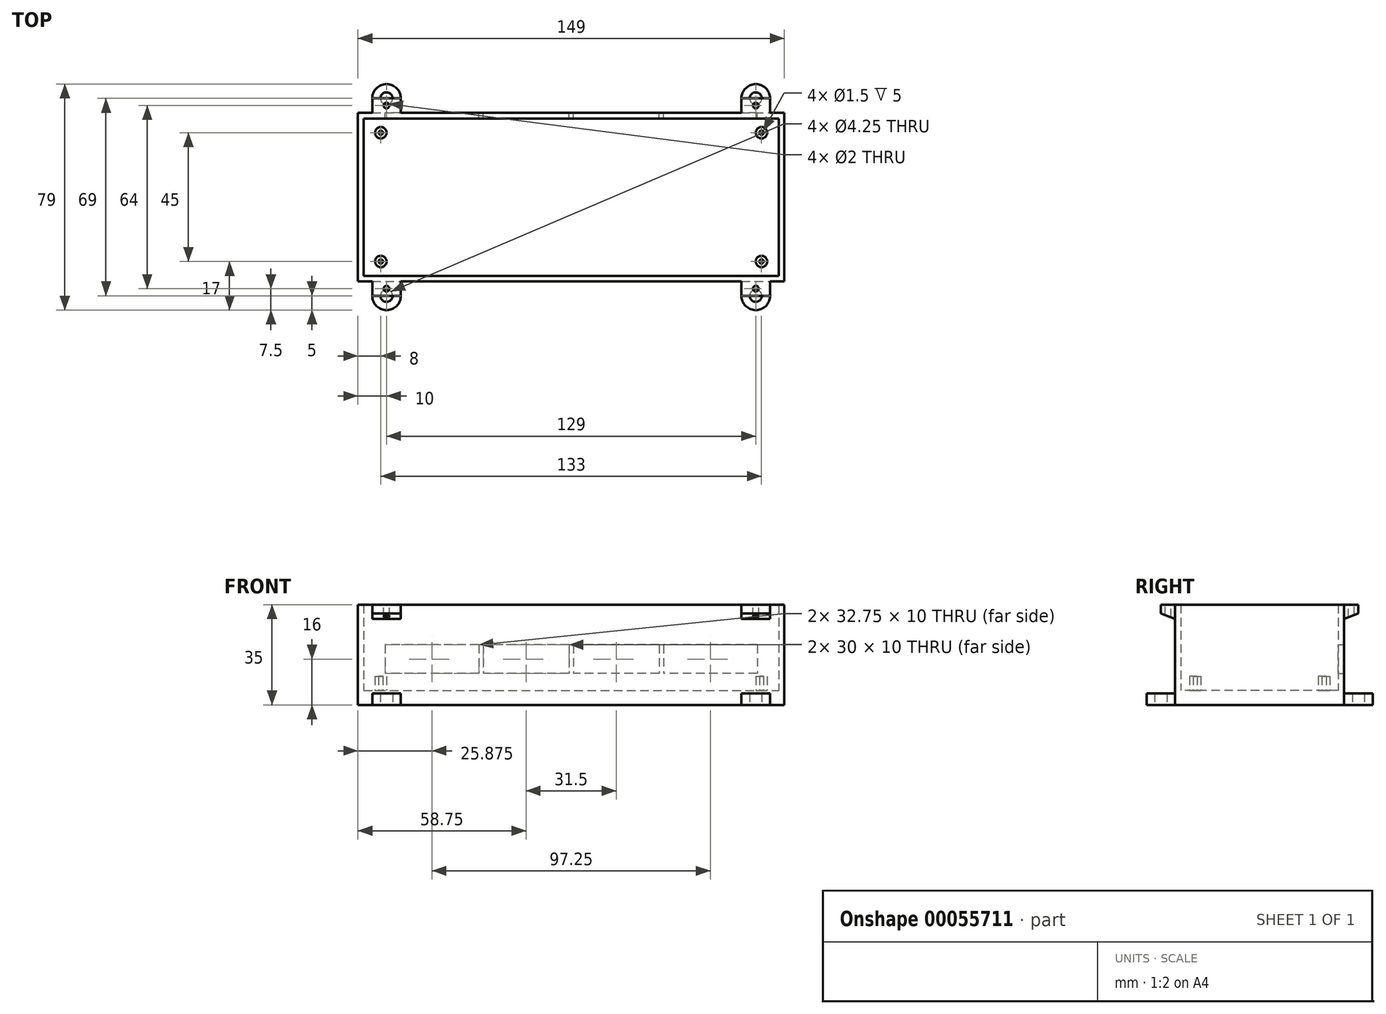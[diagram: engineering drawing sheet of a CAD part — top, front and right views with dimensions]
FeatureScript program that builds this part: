
annotation { "Feature Type Name" : "Feature", "Feature Type Description" : "" }
export const myFeature = defineFeature(function(context is Context, id is Id, definition is map)
    precondition{}
    {
        {
            var Q0;
            Q0=qCreatedBy(makeId("Top.planeOp"),FACE);
            var sketch = newSketch(context, id + "F0", { "sketchPlane" : qUnion([Q0])});
            skLineSegment(sketch, "E0.bottom", {"start": v(-72.5, 27.5) * mm, "end": v(72.5, 27.5) * mm});
            skLineSegment(sketch, "E0.top", {"start": v(-72.5, -27.5) * mm, "end": v(72.5, -27.5) * mm});
            skLineSegment(sketch, "E0.left", {"start": v(-72.5, 27.5) * mm, "end": v(-72.5, -27.5) * mm});
            skLineSegment(sketch, "E0.right", {"start": v(72.5, 27.5) * mm, "end": v(72.5, -27.5) * mm});
            skPoint(sketch, "E0.middle", {"position": v(0, 0) * mm});
            skLineSegment(sketch, "E1.bottom", {"start": v(-74.5, 29.5) * mm, "end": v(74.5, 29.5) * mm});
            skLineSegment(sketch, "E1.top", {"start": v(-74.5, -29.5) * mm, "end": v(74.5, -29.5) * mm});
            skLineSegment(sketch, "E1.left", {"start": v(-74.5, 29.5) * mm, "end": v(-74.5, -29.5) * mm});
            skLineSegment(sketch, "E1.right", {"start": v(74.5, 29.5) * mm, "end": v(74.5, -29.5) * mm});
            skSolve(sketch);
        }
        {
            var Q0;
            Q0=makeQuery(id+"F0.imprint","IMPRINT",FACE,{"disambiguationData":[TD([[makeQuery(id+"F0.imprint","IMPRINT",EDGE,{"derivedFrom":sQuery(id+"F0.wireOp",EDGE,"E0.bottom")}),1.0]])]});
            extrude(context, id + "F1", {"entities" : qUnion([Q0]), "depth" : 30 * mm});
        }
        {
            var Q0;
            Q0=makeQuery(id+"F1.opExtrude","CAP_FACE",FACE,{"disambiguationData":[OSD([sQuery(id+"F0.wireOp",EDGE,"E0.bottom"),sQuery(id+"F0.wireOp",EDGE,"E0.top"),sQuery(id+"F0.wireOp",EDGE,"E0.left"),sQuery(id+"F0.wireOp",EDGE,"E0.right"),sQuery(id+"F0.wireOp",EDGE,"E1.bottom"),sQuery(id+"F0.wireOp",EDGE,"E1.top"),sQuery(id+"F0.wireOp",EDGE,"E1.left"),sQuery(id+"F0.wireOp",EDGE,"E1.right")])],"isStart":true});
            var sketch = newSketch(context, id + "F2", { "sketchPlane" : qUnion([Q0])});
            skLineSegment(sketch, "E2.0.0", {"start": v(-74.5, -29.5) * mm, "end": v(74.5, -29.5) * mm});
            skLineSegment(sketch, "E2.0.1", {"start": v(74.5, -29.5) * mm, "end": v(74.5, 29.5) * mm});
            skLineSegment(sketch, "E2.0.2", {"start": v(74.5, 29.5) * mm, "end": v(-74.5, 29.5) * mm});
            skLineSegment(sketch, "E2.0.3", {"start": v(-74.5, 29.5) * mm, "end": v(-74.5, -29.5) * mm});
            skSolve(sketch);
        }
        {
            var Q0;
            Q0=makeQuery(id+"F2.imprint","IMPRINT",FACE,{"disambiguationData":[TD([[makeQuery(id+"F2.imprint","IMPRINT",EDGE,{"derivedFrom":sQuery(id+"F2.wireOp",EDGE,"E2.0.0")}),1.0]])]});
            var Q1;
            Q1=makeQuery(id+"F2.imprint","IMPRINT",FACE,{"disambiguationData":[TD([[makeQuery(id+"F2.imprint","IMPRINT",EDGE,{"derivedFrom":makeQuery(id+"F1.opExtrude","CAP_EDGE",EDGE,{"disambiguationData":[OSD([sQuery(id+"F0.wireOp",EDGE,"E0.bottom")])],"isStart":true})}),1.0]])]});
            extrude(context, id + "F3", {"entities" : qUnion([Q0, Q1]), "operationType" : NewBodyOperationType.ADD, "depth" : 5 * mm});
        }
        {
            var Q0;
            Q0=makeQuery(id+"F3.opExtrude","CAP_FACE",FACE,{"disambiguationData":[OSD([sQuery(id+"F2.wireOp",EDGE,"E2.0.0"),sQuery(id+"F2.wireOp",EDGE,"E2.0.1"),sQuery(id+"F2.wireOp",EDGE,"E2.0.2"),sQuery(id+"F2.wireOp",EDGE,"E2.0.3")])],"isStart":true});
            var sketch = newSketch(context, id + "F4", { "sketchPlane" : qUnion([Q0])});
            skLineSegment(sketch, "E3.bottom", {"start": v(-64.5, 22.5) * mm, "end": v(64.5, 22.5) * mm, "construction": true});
            skLineSegment(sketch, "E3.top", {"start": v(-64.5, -22.5) * mm, "end": v(64.5, -22.5) * mm, "construction": true});
            skLineSegment(sketch, "E3.left", {"start": v(-64.5, 22.5) * mm, "end": v(-64.5, -22.5) * mm, "construction": true});
            skLineSegment(sketch, "E3.right", {"start": v(64.5, 22.5) * mm, "end": v(64.5, -22.5) * mm, "construction": true});
            skPoint(sketch, "E3.middle", {"position": v(0, 0) * mm});
            skLineSegment(sketch, "E4.bottom", {"start": v(-66.5, 22.5) * mm, "end": v(66.5, 22.5) * mm, "construction": true});
            skLineSegment(sketch, "E4.top", {"start": v(-66.5, -22.5) * mm, "end": v(66.5, -22.5) * mm, "construction": true});
            skLineSegment(sketch, "E4.left", {"start": v(-66.5, 22.5) * mm, "end": v(-66.5, -22.5) * mm, "construction": true});
            skLineSegment(sketch, "E4.right", {"start": v(66.5, 22.5) * mm, "end": v(66.5, -22.5) * mm, "construction": true});
            skCircle(sketch, "E5", {"center": v(-66.5, 22.5) * mm, "radius": 2 * mm});
            skCircle(sketch, "E6", {"center": v(-66.5, -22.5) * mm, "radius": 2 * mm});
            skCircle(sketch, "E7", {"center": v(66.5, -22.5) * mm, "radius": 2 * mm});
            skCircle(sketch, "E8", {"center": v(66.5, 22.5) * mm, "radius": 2 * mm});
            skLineSegment(sketch, "E9.bottom", {"start": v(-66.5, 20.5) * mm, "end": v(66.5, 20.5) * mm, "construction": true});
            skLineSegment(sketch, "E9.top", {"start": v(-66.5, -20.5) * mm, "end": v(66.5, -20.5) * mm, "construction": true});
            skLineSegment(sketch, "E9.left", {"start": v(-66.5, 20.5) * mm, "end": v(-66.5, -20.5) * mm, "construction": true});
            skLineSegment(sketch, "E9.right", {"start": v(66.5, 20.5) * mm, "end": v(66.5, -20.5) * mm, "construction": true});
            skCircle(sketch, "E10", {"center": v(-66.5, 22.5) * mm, "radius": 0.75 * mm});
            skCircle(sketch, "E11", {"center": v(-66.5, -22.5) * mm, "radius": 0.75 * mm});
            skCircle(sketch, "E12", {"center": v(66.5, -22.5) * mm, "radius": 0.75 * mm});
            skCircle(sketch, "E13", {"center": v(66.5, 22.5) * mm, "radius": 0.75 * mm});
            skSolve(sketch);
        }
        {
            var Q0;
            Q0=makeQuery(id+"F4.imprint","IMPRINT",FACE,{"disambiguationData":[TD([[makeQuery(id+"F4.imprint","IMPRINT",EDGE,{"derivedFrom":sQuery(id+"F4.wireOp",EDGE,"E5")}),1.0]])]});
            var Q1;
            Q1=makeQuery(id+"F4.imprint","IMPRINT",FACE,{"disambiguationData":[TD([[makeQuery(id+"F4.imprint","IMPRINT",EDGE,{"derivedFrom":sQuery(id+"F4.wireOp",EDGE,"E6")}),1.0]])]});
            var Q2;
            Q2=makeQuery(id+"F4.imprint","IMPRINT",FACE,{"disambiguationData":[TD([[makeQuery(id+"F4.imprint","IMPRINT",EDGE,{"derivedFrom":sQuery(id+"F4.wireOp",EDGE,"E7")}),1.0]])]});
            var Q3;
            Q3=makeQuery(id+"F4.imprint","IMPRINT",FACE,{"disambiguationData":[TD([[makeQuery(id+"F4.imprint","IMPRINT",EDGE,{"derivedFrom":sQuery(id+"F4.wireOp",EDGE,"E8")}),1.0]])]});
            extrude(context, id + "F5", {"entities" : qUnion([Q0, Q1, Q2, Q3]), "operationType" : NewBodyOperationType.ADD, "depth" : 5 * mm});
        }
        {
            var Q0;
            Q0=makeQuery(id+"F3.opExtrude","CAP_FACE",FACE,{"disambiguationData":[OSD([sQuery(id+"F2.wireOp",EDGE,"E2.0.0"),sQuery(id+"F2.wireOp",EDGE,"E2.0.1"),sQuery(id+"F2.wireOp",EDGE,"E2.0.2"),sQuery(id+"F2.wireOp",EDGE,"E2.0.3")])],"isStart":false});
            var sketch = newSketch(context, id + "F6", { "sketchPlane" : qUnion([Q0])});
            skLineSegment(sketch, "E14.bottom", {"start": v(-69.5, 29.5) * mm, "end": v(-59.5, 29.5) * mm});
            skLineSegment(sketch, "E14.top", {"start": v(-69.5, 39.5) * mm, "end": v(-59.5, 39.5) * mm});
            skLineSegment(sketch, "E14.left", {"start": v(-69.5, 29.5) * mm, "end": v(-69.5, 39.5) * mm});
            skLineSegment(sketch, "E14.right", {"start": v(-59.5, 29.5) * mm, "end": v(-59.5, 39.5) * mm});
            skCircle(sketch, "E15", {"center": v(-64.5, 34.5) * mm, "radius": 2.12 * mm});
            skLineSegment(sketch, "E16", {"start": v(-64.5, 39.5) * mm, "end": v(-64.5, 29.5) * mm, "construction": true});
            skLineSegment(sketch, "E17", {"start": v(0, -29.5) * mm, "end": v(0, 29.5) * mm, "construction": true});
            skLineSegment(sketch, "E18", {"start": v(-74.5, 0) * mm, "end": v(74.5, 0) * mm, "construction": true});
            skLineSegment(sketch, "E19.MirrorCS", {"start": v(59.5, 29.5) * mm, "end": v(59.5, 39.5) * mm});
            skLineSegment(sketch, "E20.MirrorCS", {"start": v(69.5, 39.5) * mm, "end": v(59.5, 39.5) * mm});
            skCircle(sketch, "E21.MirrorC", {"center": v(64.5, 34.5) * mm, "radius": 2.12 * mm});
            skLineSegment(sketch, "E22.MirrorCS", {"start": v(69.5, 29.5) * mm, "end": v(59.5, 29.5) * mm});
            skLineSegment(sketch, "E23.MirrorCS", {"start": v(69.5, 29.5) * mm, "end": v(69.5, 39.5) * mm});
            skLineSegment(sketch, "E24.MirrorCS", {"start": v(-59.5, -29.5) * mm, "end": v(-59.5, -39.5) * mm});
            skLineSegment(sketch, "E25.MirrorCS", {"start": v(-69.5, -29.5) * mm, "end": v(-59.5, -29.5) * mm});
            skLineSegment(sketch, "E26.MirrorCS", {"start": v(-69.5, -29.5) * mm, "end": v(-69.5, -39.5) * mm});
            skLineSegment(sketch, "E27.MirrorCS", {"start": v(-69.5, -39.5) * mm, "end": v(-59.5, -39.5) * mm});
            skCircle(sketch, "E28.MirrorC", {"center": v(-64.5, -34.5) * mm, "radius": 2.12 * mm});
            skLineSegment(sketch, "E29.MirrorCS", {"start": v(59.5, -29.5) * mm, "end": v(59.5, -39.5) * mm});
            skCircle(sketch, "E30.MirrorC", {"center": v(64.5, -34.5) * mm, "radius": 2.12 * mm});
            skLineSegment(sketch, "E31.MirrorCS", {"start": v(69.5, -29.5) * mm, "end": v(59.5, -29.5) * mm});
            skLineSegment(sketch, "E32.MirrorCS", {"start": v(69.5, -29.5) * mm, "end": v(69.5, -39.5) * mm});
            skLineSegment(sketch, "E33.MirrorCS", {"start": v(69.5, -39.5) * mm, "end": v(59.5, -39.5) * mm});
            skSolve(sketch);
        }
        {
            var Q0;
            Q0 = qSketchRegion(id + "F6", true);
            extrude(context, id + "F7", {"entities" : qUnion([Q0]), "operationType" : NewBodyOperationType.ADD, "oppositeDirection" : true, "depth" : 4 * mm});
        }
        {
            var Q0;
            Q0=makeQuery(id+"F7.opExtrude","SWEPT_EDGE",EDGE,{"disambiguationData":[OSD([sQuery(id+"F6.wireOp",EDGE,"E14.top"),sQuery(id+"F6.wireOp",EDGE,"E14.left")])]});
            var Q1;
            Q1=makeQuery(id+"F7.opExtrude","SWEPT_EDGE",EDGE,{"disambiguationData":[OSD([sQuery(id+"F6.wireOp",EDGE,"E14.top"),sQuery(id+"F6.wireOp",EDGE,"E14.right")])]});
            var Q2;
            Q2=makeQuery(id+"F7.opExtrude","SWEPT_EDGE",EDGE,{"disambiguationData":[OSD([sQuery(id+"F6.wireOp",EDGE,"E20.MirrorCS"),sQuery(id+"F6.wireOp",EDGE,"E23.MirrorCS")])]});
            var Q3;
            Q3=makeQuery(id+"F7.opExtrude","SWEPT_EDGE",EDGE,{"disambiguationData":[OSD([sQuery(id+"F6.wireOp",EDGE,"E19.MirrorCS"),sQuery(id+"F6.wireOp",EDGE,"E20.MirrorCS")])]});
            var Q4;
            Q4=makeQuery(id+"F7.opExtrude","SWEPT_EDGE",EDGE,{"disambiguationData":[OSD([sQuery(id+"F6.wireOp",EDGE,"E32.MirrorCS"),sQuery(id+"F6.wireOp",EDGE,"E33.MirrorCS")])]});
            var Q5;
            Q5=makeQuery(id+"F7.opExtrude","SWEPT_EDGE",EDGE,{"disambiguationData":[OSD([sQuery(id+"F6.wireOp",EDGE,"E29.MirrorCS"),sQuery(id+"F6.wireOp",EDGE,"E33.MirrorCS")])]});
            var Q6;
            Q6=makeQuery(id+"F7.opExtrude","SWEPT_EDGE",EDGE,{"disambiguationData":[OSD([sQuery(id+"F6.wireOp",EDGE,"E24.MirrorCS"),sQuery(id+"F6.wireOp",EDGE,"E27.MirrorCS")])]});
            var Q7;
            Q7=makeQuery(id+"F7.opExtrude","SWEPT_EDGE",EDGE,{"disambiguationData":[OSD([sQuery(id+"F6.wireOp",EDGE,"E26.MirrorCS"),sQuery(id+"F6.wireOp",EDGE,"E27.MirrorCS")])]});
            fillet(context, id + "F8", {"entities" : qUnion([Q0, Q1, Q2, Q3, Q4, Q5, Q6, Q7]), "radius" : 5 * mm, "tangentPropagation" : true, "allowEdgeOverflow" : false});
        }
        {
            var Q0;
            Q0=makeQuery(id+"F3.boolean.opBoolean","MERGE",FACE,{"derivedFrom":[makeQuery(id+"F1.opExtrude","SWEPT_FACE",FACE,{"disambiguationData":[OSD([sQuery(id+"F0.wireOp",EDGE,"E1.bottom")])]}),makeQuery(id+"F3.opExtrude","SWEPT_FACE",FACE,{"disambiguationData":[OSD([sQuery(id+"F2.wireOp",EDGE,"E2.0.0")])]})]});
            var sketch = newSketch(context, id + "F9", { "sketchPlane" : qUnion([Q0])});
            skLineSegment(sketch, "E34.bottom", {"start": v(-65, 16) * mm, "end": v(65, 16) * mm});
            skLineSegment(sketch, "E34.top", {"start": v(-65, 6) * mm, "end": v(65, 6) * mm});
            skLineSegment(sketch, "E34.left", {"start": v(-65, 16) * mm, "end": v(-65, 6) * mm});
            skLineSegment(sketch, "E34.right", {"start": v(65, 16) * mm, "end": v(65, 6) * mm});
            skLineSegment(sketch, "E35.0", {"start": v(-68.5, 5) * mm, "end": v(-64.5, 5) * mm});
            skLineSegment(sketch, "E36.0", {"start": v(64.5, 5) * mm, "end": v(68.5, 5) * mm});
            skLineSegment(sketch, "E37", {"start": v(0, 30) * mm, "end": v(0, 6) * mm, "construction": true});
            skPoint(sketch, "E37.endSnap0", {"position": v(0, 6) * mm});
            skLineSegment(sketch, "E38.bottom", {"start": v(-32.25, 16) * mm, "end": v(-30.75, 16) * mm});
            skLineSegment(sketch, "E38.top", {"start": v(-32.25, 6) * mm, "end": v(-30.75, 6) * mm});
            skLineSegment(sketch, "E38.left", {"start": v(-32.25, 16) * mm, "end": v(-32.25, 6) * mm});
            skLineSegment(sketch, "E38.right", {"start": v(-30.75, 16) * mm, "end": v(-30.75, 6) * mm});
            skLineSegment(sketch, "E39.bottom", {"start": v(-0.75, 16) * mm, "end": v(0.75, 16) * mm});
            skLineSegment(sketch, "E39.top", {"start": v(-0.75, 6) * mm, "end": v(0.75, 6) * mm});
            skLineSegment(sketch, "E39.left", {"start": v(-0.75, 16) * mm, "end": v(-0.75, 6) * mm});
            skLineSegment(sketch, "E39.right", {"start": v(0.75, 16) * mm, "end": v(0.75, 6) * mm});
            skLineSegment(sketch, "E40.bottom", {"start": v(30.75, 16) * mm, "end": v(32.25, 16) * mm});
            skLineSegment(sketch, "E40.top", {"start": v(30.75, 6) * mm, "end": v(32.25, 6) * mm});
            skLineSegment(sketch, "E40.left", {"start": v(30.75, 16) * mm, "end": v(30.75, 6) * mm});
            skLineSegment(sketch, "E40.right", {"start": v(32.25, 16) * mm, "end": v(32.25, 6) * mm});
            skLineSegment(sketch, "E41", {"start": v(-31.5, 16) * mm, "end": v(-31.5, 6) * mm, "construction": true});
            skLineSegment(sketch, "E42", {"start": v(31.5, 16) * mm, "end": v(31.5, 6) * mm, "construction": true});
            skSolve(sketch);
        }
        {
            var Q0;
            {var subQ0=sQuery(id+"F9.wireOp",EDGE,"E34.left");Q0=makeQuery(id+"F9.imprint","IMPRINT",FACE,{"disambiguationData":[TD([[makeQuery(id+"F9.imprint","IMPRINT",EDGE,{"derivedFrom":subQ0}),1.0]])]});}
            var Q1;
            {var subQ0=sQuery(id+"F9.wireOp",EDGE,"E38.right");Q1=makeQuery(id+"F9.imprint","IMPRINT",FACE,{"disambiguationData":[TD([[makeQuery(id+"F9.imprint","IMPRINT",EDGE,{"derivedFrom":subQ0}),1.0]])]});}
            var Q2;
            {var subQ0=sQuery(id+"F9.wireOp",EDGE,"E39.right");Q2=makeQuery(id+"F9.imprint","IMPRINT",FACE,{"disambiguationData":[TD([[makeQuery(id+"F9.imprint","IMPRINT",EDGE,{"derivedFrom":subQ0}),1.0]])]});}
            var Q3;
            {var subQ0=sQuery(id+"F9.wireOp",EDGE,"E34.right");Q3=makeQuery(id+"F9.imprint","IMPRINT",FACE,{"disambiguationData":[TD([[makeQuery(id+"F9.imprint","IMPRINT",EDGE,{"derivedFrom":subQ0}),-1.0]])]});}
            extrude(context, id + "F10", {"entities" : qUnion([Q0, Q1, Q2, Q3]), "operationType" : NewBodyOperationType.REMOVE, "endBound" : BoundingType.UP_TO_NEXT, "oppositeDirection" : true, "depth" : 25 * mm});
        }
        {
            var Q0;
            Q0=makeQuery(id+"F1.opExtrude","CAP_FACE",FACE,{"disambiguationData":[OSD([sQuery(id+"F0.wireOp",EDGE,"E0.bottom"),sQuery(id+"F0.wireOp",EDGE,"E0.top"),sQuery(id+"F0.wireOp",EDGE,"E0.left"),sQuery(id+"F0.wireOp",EDGE,"E0.right"),sQuery(id+"F0.wireOp",EDGE,"E1.bottom"),sQuery(id+"F0.wireOp",EDGE,"E1.top"),sQuery(id+"F0.wireOp",EDGE,"E1.left"),sQuery(id+"F0.wireOp",EDGE,"E1.right")])],"isStart":false});
            var sketch = newSketch(context, id + "F11", { "sketchPlane" : qUnion([Q0])});
            skLineSegment(sketch, "E43.0", {"start": v(-69.5, 29.5) * mm, "end": v(-69.5, 34.5) * mm});
            skLineSegment(sketch, "E44.0", {"start": v(-74.5, 29.5) * mm, "end": v(74.5, 29.5) * mm});
            skLineSegment(sketch, "E45.0", {"start": v(-59.5, 29.5) * mm, "end": v(-59.5, 34.5) * mm});
            skLineSegment(sketch, "E46.0", {"start": v(59.5, 29.5) * mm, "end": v(59.5, 34.5) * mm});
            skLineSegment(sketch, "E47.0", {"start": v(69.5, 29.5) * mm, "end": v(69.5, 34.5) * mm});
            skLineSegment(sketch, "E48.0", {"start": v(69.5, -29.5) * mm, "end": v(69.5, -34.5) * mm});
            skLineSegment(sketch, "E49.0", {"start": v(-74.5, -29.5) * mm, "end": v(74.5, -29.5) * mm});
            skLineSegment(sketch, "E50.0", {"start": v(59.5, -29.5) * mm, "end": v(59.5, -34.5) * mm});
            skLineSegment(sketch, "E51.0", {"start": v(-59.5, -29.5) * mm, "end": v(-59.5, -34.5) * mm});
            skLineSegment(sketch, "E52.0", {"start": v(-69.5, -29.5) * mm, "end": v(-69.5, -34.5) * mm});
            skLineSegment(sketch, "E53", {"start": v(-69.5, 34.5) * mm, "end": v(-59.5, 34.5) * mm});
            skLineSegment(sketch, "E54", {"start": v(59.5, 34.5) * mm, "end": v(69.5, 34.5) * mm});
            skLineSegment(sketch, "E55", {"start": v(59.5, -34.5) * mm, "end": v(69.5, -34.5) * mm});
            skLineSegment(sketch, "E56", {"start": v(-69.5, -34.5) * mm, "end": v(-59.5, -34.5) * mm});
            skSolve(sketch);
        }
        {
            var Q0;
            Q0 = qSketchRegion(id + "F11", true);
            extrude(context, id + "F12", {"entities" : qUnion([Q0]), "operationType" : NewBodyOperationType.ADD, "oppositeDirection" : true, "depth" : 5 * mm});
        }
        {
            var Q0;
            Q0=makeQuery(id+"F12.opExtrude","SWEPT_FACE",FACE,{"disambiguationData":[OSD([sQuery(id+"F11.wireOp",EDGE,"E52.0")])]});
            var sketch = newSketch(context, id + "F13", { "sketchPlane" : qUnion([Q0])});
            skLineSegment(sketch, "E57", {"start": v(29.5, 25) * mm, "end": v(34.5, 27) * mm});
            skLineSegment(sketch, "E58", {"start": v(34.5, 27) * mm, "end": v(34.5, 25) * mm});
            skLineSegment(sketch, "E59", {"start": v(34.5, 25) * mm, "end": v(29.5, 25) * mm});
            skLineSegment(sketch, "E60", {"start": v(-34.5, 27) * mm, "end": v(-29.5, 25) * mm});
            skLineSegment(sketch, "E61", {"start": v(-29.5, 25) * mm, "end": v(-34.5, 25) * mm});
            skLineSegment(sketch, "E62", {"start": v(-34.5, 25) * mm, "end": v(-34.5, 27) * mm});
            skLineSegment(sketch, "E63.0", {"start": v(-34.5, 25) * mm, "end": v(-34.5, 30) * mm});
            skLineSegment(sketch, "E64.0", {"start": v(-29.5, 30) * mm, "end": v(-29.5, -5) * mm});
            skLineSegment(sketch, "E65.0", {"start": v(29.5, 30) * mm, "end": v(29.5, -5) * mm});
            skSolve(sketch);
        }
        {
            var Q0;
            Q0 = qSketchRegion(id + "F13", true);
            extrude(context, id + "F14", {"entities" : qUnion([Q0]), "operationType" : NewBodyOperationType.REMOVE, "endBound" : BoundingType.THROUGH_ALL, "oppositeDirection" : true, "depth" : 25 * mm});
        }
        {
            var Q0;
            {var subQ0=sQuery(id+"F11.wireOp",EDGE,"E49.0");var subQ1=sQuery(id+"F11.wireOp",EDGE,"E44.0");Q0=makeQuery(id+"F12.boolean.opBoolean","MERGE",FACE,{"derivedFrom":[makeQuery(id+"F1.opExtrude","CAP_FACE",FACE,{"disambiguationData":[OSD([sQuery(id+"F0.wireOp",EDGE,"E0.bottom"),sQuery(id+"F0.wireOp",EDGE,"E0.top"),sQuery(id+"F0.wireOp",EDGE,"E0.left"),sQuery(id+"F0.wireOp",EDGE,"E0.right"),sQuery(id+"F0.wireOp",EDGE,"E1.bottom"),sQuery(id+"F0.wireOp",EDGE,"E1.top"),sQuery(id+"F0.wireOp",EDGE,"E1.left"),sQuery(id+"F0.wireOp",EDGE,"E1.right")])],"isStart":false}),makeQuery(id+"F12.opExtrude","CAP_FACE",FACE,{"disambiguationData":[OSD([sQuery(id+"F11.wireOp",EDGE,"E43.0"),subQ1,sQuery(id+"F11.wireOp",EDGE,"E45.0"),sQuery(id+"F11.wireOp",EDGE,"E53")])],"isStart":true}),makeQuery(id+"F12.opExtrude","CAP_FACE",FACE,{"disambiguationData":[OSD([subQ1,sQuery(id+"F11.wireOp",EDGE,"E46.0"),sQuery(id+"F11.wireOp",EDGE,"E47.0"),sQuery(id+"F11.wireOp",EDGE,"E54")])],"isStart":true}),makeQuery(id+"F12.opExtrude","CAP_FACE",FACE,{"disambiguationData":[OSD([sQuery(id+"F11.wireOp",EDGE,"E48.0"),subQ0,sQuery(id+"F11.wireOp",EDGE,"E50.0"),sQuery(id+"F11.wireOp",EDGE,"E55")])],"isStart":true}),makeQuery(id+"F12.opExtrude","CAP_FACE",FACE,{"disambiguationData":[OSD([subQ0,sQuery(id+"F11.wireOp",EDGE,"E51.0"),sQuery(id+"F11.wireOp",EDGE,"E52.0"),sQuery(id+"F11.wireOp",EDGE,"E56")])],"isStart":true})]});}
            var sketch = newSketch(context, id + "F15", { "sketchPlane" : qUnion([Q0])});
            skPoint(sketch, "E66.firstSnap0", {"position": v(-64.5, 34.5) * mm});
            skPoint(sketch, "E66.oppositeSnap0", {"position": v(64.5, -34.5) * mm});
            skLineSegment(sketch, "E66.bottom", {"start": v(-64.5, 32) * mm, "end": v(64.5, 32) * mm});
            skLineSegment(sketch, "E66.top", {"start": v(-64.5, -32) * mm, "end": v(64.5, -32) * mm});
            skLineSegment(sketch, "E66.left", {"start": v(-64.5, 32) * mm, "end": v(-64.5, -32) * mm});
            skLineSegment(sketch, "E66.right", {"start": v(64.5, 32) * mm, "end": v(64.5, -32) * mm});
            skLineSegment(sketch, "E67", {"start": v(-69.5, 32) * mm, "end": v(-59.5, 32) * mm, "construction": true});
            skLineSegment(sketch, "E68", {"start": v(69.5, -32) * mm, "end": v(59.5, -32) * mm, "construction": true});
            skSolve(sketch);
        }
        {
            var Q0;
            Q0=sQuery(id+"F15.wireOp",VERTEX,"E66.right.start");
            var Q1;
            Q1=sQuery(id+"F15.wireOp",VERTEX,"E66.right.end");
            var Q2;
            Q2=sQuery(id+"F15.wireOp",VERTEX,"E66.left.end");
            var Q3;
            Q3=sQuery(id+"F15.wireOp",VERTEX,"E66.left.start");
            var Q4;
            Q4=makeQuery(id+"F1.opExtrude","SWEPT_BODY",BODY,{"disambiguationData":[OSD([sQuery(id+"F0.wireOp",EDGE,"E0.bottom"),sQuery(id+"F0.wireOp",EDGE,"E0.top"),sQuery(id+"F0.wireOp",EDGE,"E0.left"),sQuery(id+"F0.wireOp",EDGE,"E0.right"),sQuery(id+"F0.wireOp",EDGE,"E1.bottom"),sQuery(id+"F0.wireOp",EDGE,"E1.top"),sQuery(id+"F0.wireOp",EDGE,"E1.left"),sQuery(id+"F0.wireOp",EDGE,"E1.right")])]});
            hole(context, id + "F16", {"style" : HoleStyle.SIMPLE, "holeDiameter" : 2 * mm, "endStyle" : HoleEndStyle.BLIND, "holeDepth" : 5 * mm, "locations" : qUnion([Q0, Q1, Q2, Q3]), "scope" : qUnion([Q4])});
        }
    });
